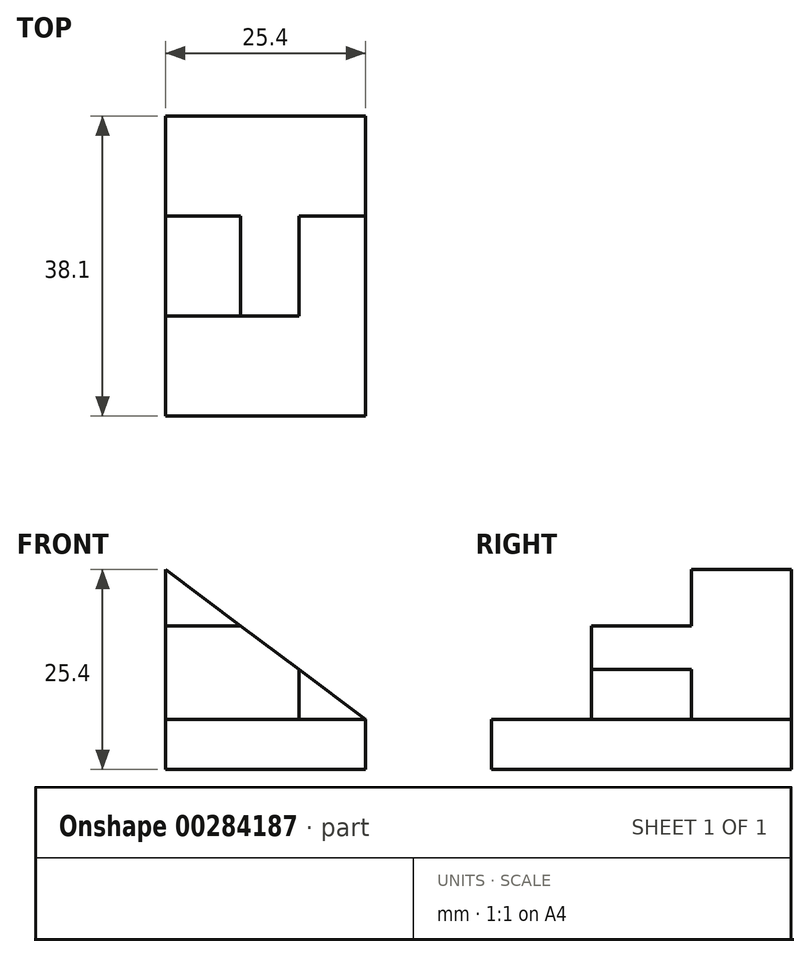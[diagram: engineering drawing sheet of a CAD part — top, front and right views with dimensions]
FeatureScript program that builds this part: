
annotation { "Feature Type Name" : "Feature", "Feature Type Description" : "" }
export const myFeature = defineFeature(function(context is Context, id is Id, definition is map)
    precondition{}
    {
        {
            var Q0;
            Q0=qCreatedBy(makeId("Front.planeOp"),FACE);
            var sketch = newSketch(context, id + "F0", { "sketchPlane" : qUnion([Q0])});
            skLineSegment(sketch, "E0", {"start": v(0, 0) * mm, "end": v(0, 19.05) * mm});
            skLineSegment(sketch, "E1", {"start": v(0, 19.05) * mm, "end": v(25.4, 0) * mm});
            skLineSegment(sketch, "E2", {"start": v(25.4, 0) * mm, "end": v(0, 0) * mm});
            skLineSegment(sketch, "E3", {"start": v(0, 0) * mm, "end": v(0, -6.35) * mm});
            skLineSegment(sketch, "E4", {"start": v(0, -6.35) * mm, "end": v(25.4, -6.35) * mm});
            skLineSegment(sketch, "E5", {"start": v(25.4, -6.35) * mm, "end": v(25.4, 0) * mm});
            skSolve(sketch);
        }
        {
            var Q0;
            Q0=makeQuery(id+"F0.imprint","IMPRINT",FACE,{"disambiguationData":[TD([[makeQuery(id+"F0.imprint","IMPRINT",EDGE,{"derivedFrom":sQuery(id+"F0.wireOp",EDGE,"E2")}),1.0]])]});
            extrude(context, id + "F1", {"entities" : qUnion([Q0]), "depth" : 38.1 * mm});
        }
        {
            var Q0;
            Q0=makeQuery(id+"F0.imprint","IMPRINT",FACE,{"disambiguationData":[TD([[makeQuery(id+"F0.imprint","IMPRINT",EDGE,{"derivedFrom":sQuery(id+"F0.wireOp",EDGE,"E0")}),-1.0]])]});
            extrude(context, id + "F2", {"entities" : qUnion([Q0]), "operationType" : NewBodyOperationType.ADD, "depth" : 12.7 * mm});
        }
        {
            var Q0;
            Q0=makeQuery(id+"F2.opExtrude","CAP_FACE",FACE,{"disambiguationData":[OSD([sQuery(id+"F0.wireOp",EDGE,"E0"),sQuery(id+"F0.wireOp",EDGE,"E1"),sQuery(id+"F0.wireOp",EDGE,"E2")])],"isStart":false});
            var sketch = newSketch(context, id + "F3", { "sketchPlane" : qUnion([Q0])});
            skLineSegment(sketch, "E6", {"start": v(0, 0) * mm, "end": v(0, 11.9) * mm});
            skLineSegment(sketch, "E7", {"start": v(0, 11.9) * mm, "end": v(9.53, 11.9) * mm});
            skLineSegment(sketch, "E8", {"start": v(9.53, 11.9) * mm, "end": v(16.93, 6.35) * mm});
            skLineSegment(sketch, "E9", {"start": v(16.93, 6.35) * mm, "end": v(16.93, 0) * mm});
            skLineSegment(sketch, "E10", {"start": v(0, 0) * mm, "end": v(16.93, 0) * mm});
            skSolve(sketch);
        }
        {
            var Q0;
            Q0=makeQuery(id+"F3.imprint","IMPRINT",FACE,{"disambiguationData":[TD([[makeQuery(id+"F3.imprint","IMPRINT",EDGE,{"derivedFrom":sQuery(id+"F3.wireOp",EDGE,"E6")}),-1.0]])]});
            extrude(context, id + "F4", {"entities" : qUnion([Q0]), "operationType" : NewBodyOperationType.ADD, "depth" : 12.7 * mm});
        }
    });
